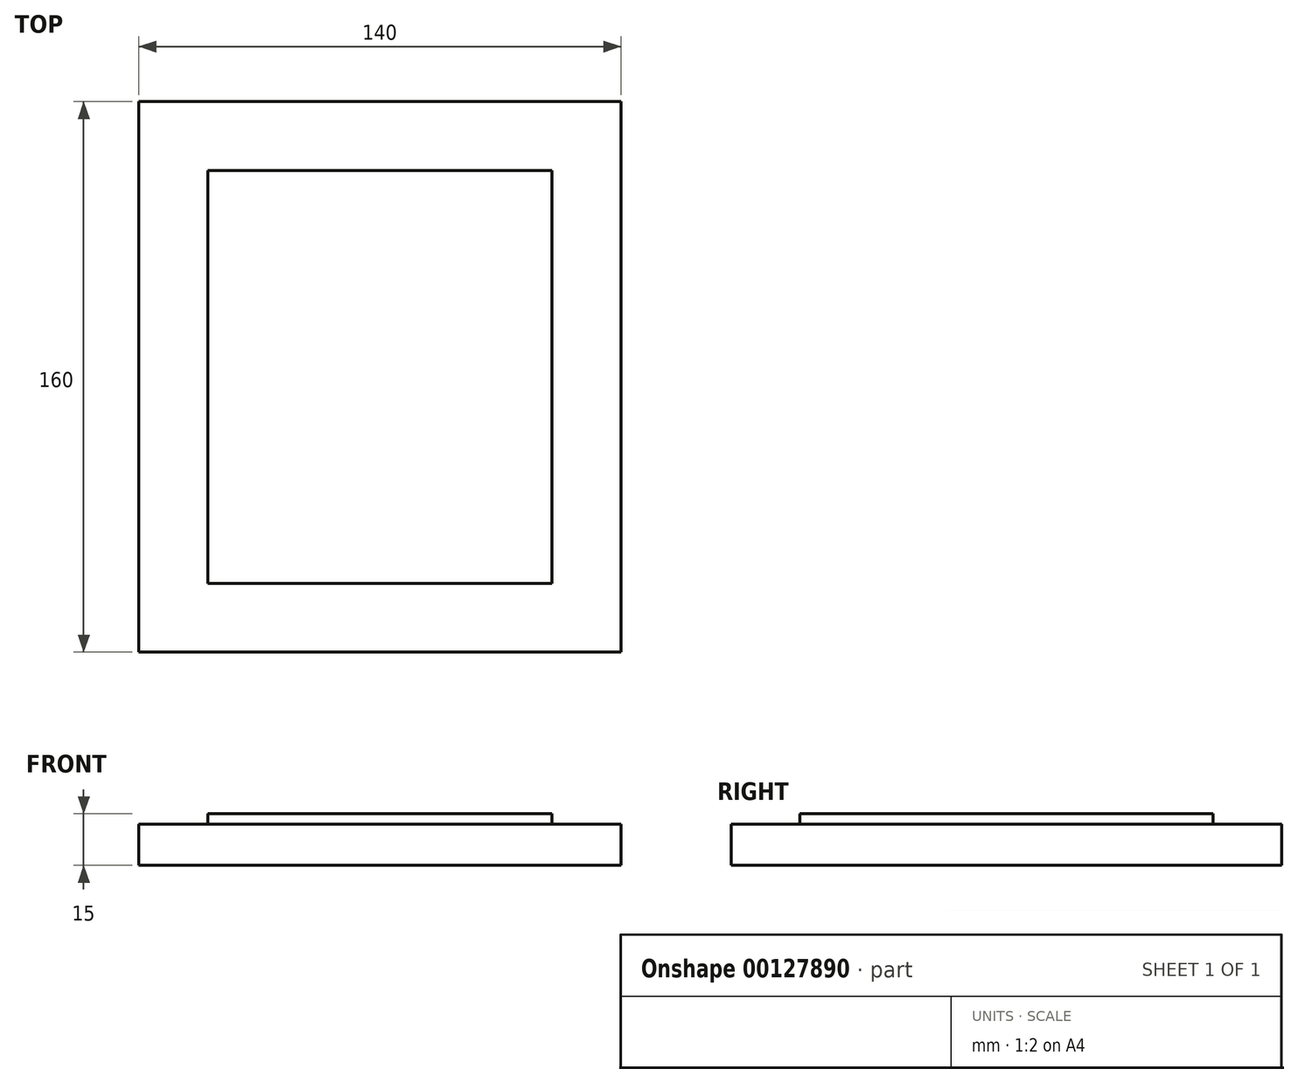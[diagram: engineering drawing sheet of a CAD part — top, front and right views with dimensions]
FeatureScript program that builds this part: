
annotation { "Feature Type Name" : "Feature", "Feature Type Description" : "" }
export const myFeature = defineFeature(function(context is Context, id is Id, definition is map)
    precondition{}
    {
        {
            var Q0;
            Q0=qCreatedBy(makeId("Top.planeOp"),FACE);
            var sketch = newSketch(context, id + "F0", { "sketchPlane" : qUnion([Q0])});
            skLineSegment(sketch, "E0.bottom", {"start": v(-20, -20) * mm, "end": v(120, -20) * mm});
            skLineSegment(sketch, "E0.top", {"start": v(-20, 140) * mm, "end": v(120, 140) * mm});
            skLineSegment(sketch, "E0.left", {"start": v(-20, -20) * mm, "end": v(-20, 140) * mm});
            skLineSegment(sketch, "E0.right", {"start": v(120, -20) * mm, "end": v(120, 140) * mm});
            skLineSegment(sketch, "E1.bottom", {"start": v(0, 0) * mm, "end": v(100, 0) * mm});
            skLineSegment(sketch, "E1.top", {"start": v(0, 120) * mm, "end": v(100, 120) * mm});
            skLineSegment(sketch, "E1.left", {"start": v(0, 0) * mm, "end": v(0, 120) * mm});
            skLineSegment(sketch, "E1.right", {"start": v(100, 0) * mm, "end": v(100, 120) * mm});
            skSolve(sketch);
        }
        {
            var Q0;
            Q0 = qSketchRegion(id + "F0", true);
            var Q1;
            Q1=makeQuery(id+"F0.imprint","IMPRINT",FACE,{"disambiguationData":[TD([[makeQuery(id+"F0.imprint","IMPRINT",EDGE,{"derivedFrom":sQuery(id+"F0.wireOp",EDGE,"E1.bottom")}),1.0]])]});
            extrude(context, id + "F1", {"entities" : qUnion([Q0, Q1]), "depth" : 2 * mm});
        }
        {
            var Q0;
            Q0=makeQuery(id+"F0.imprint","IMPRINT",FACE,{"disambiguationData":[TD([[makeQuery(id+"F0.imprint","IMPRINT",EDGE,{"derivedFrom":sQuery(id+"F0.wireOp",EDGE,"E1.bottom")}),1.0]])]});
            extrude(context, id + "F2", {"entities" : qUnion([Q0]), "operationType" : NewBodyOperationType.ADD, "depth" : 5 * mm});
        }
        {
            var Q0;
            Q0=makeQuery(id+"F0.imprint","IMPRINT",FACE,{"disambiguationData":[TD([[makeQuery(id+"F0.imprint","IMPRINT",EDGE,{"derivedFrom":sQuery(id+"F0.wireOp",EDGE,"E0.bottom")}),1.0]])]});
            var Q1;
            Q1=makeQuery(id+"F0.imprint","IMPRINT",FACE,{"disambiguationData":[TD([[makeQuery(id+"F0.imprint","IMPRINT",EDGE,{"derivedFrom":sQuery(id+"F0.wireOp",EDGE,"E1.bottom")}),1.0]])]});
            extrude(context, id + "F3", {"entities" : qUnion([Q0, Q1]), "operationType" : NewBodyOperationType.ADD, "oppositeDirection" : true, "depth" : 10 * mm});
        }
    });
